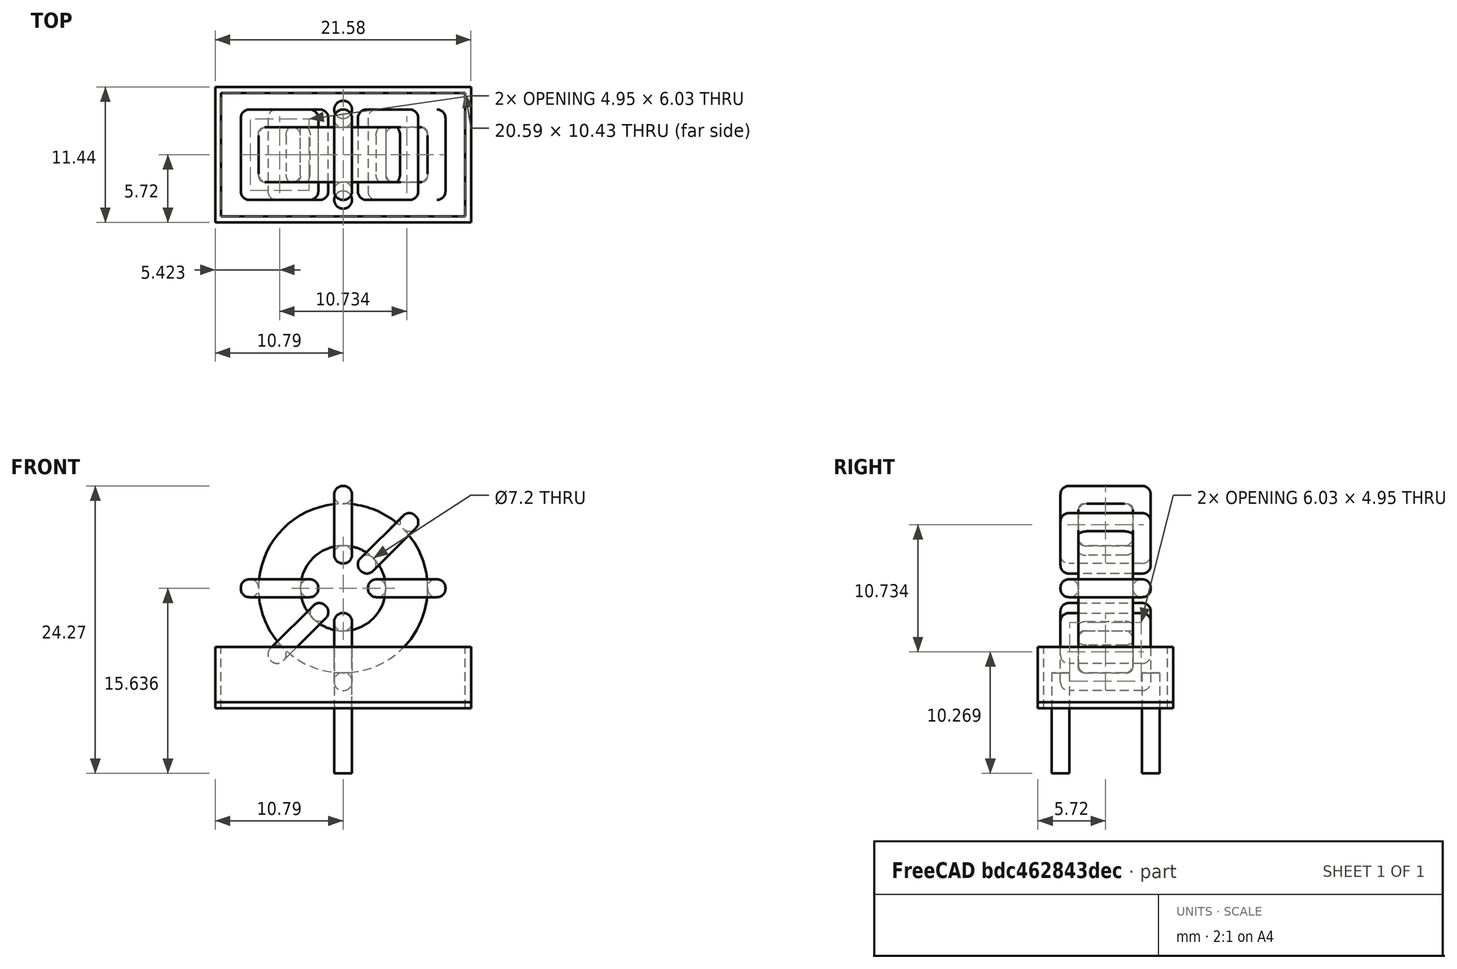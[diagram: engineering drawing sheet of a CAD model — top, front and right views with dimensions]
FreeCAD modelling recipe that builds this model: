
FCSTD DOCUMENT  (FreeCAD 0.16R6703 (Git))
Label: L_Toroid_Vertical_L21.6mm_W11.4mm_P7.62mm_Pulse_KM-3
License: All rights reserved
LicenseURL: http://en.wikipedia.org/wiki/All_rights_reserved
objects: Sketcher::SketchObject×8, PartDesign::Pad×8, PartDesign::Fillet×5, Spreadsheet::Sheet×1
note: 29 computed .brp shape members not serialized (recipe doc carries the construction recipe); baked Part::Feature solids carry a one-line shape summary decoded from their .brp

FEATURE [Spreadsheet::Sheet] Spreadsheet  label="dimensions"
  cells = A1=Wx; B1(Wx)=17.272; C1(WW)=7.196666666666666; D1(iWx)=21.59; A2=Wy; B2(Wy)=7.62; D2(iWy)=11.43; A3=RM; B3(RMx)=7.62; C3(RMy)=0; A4=d_wire; B4(d_wire)=1.5; A5=H; B5(H)=21.59; A6=offsetx; B6(offsetx)=10.795
FEATURE [Sketcher::SketchObject] Sketch
  Placement = pos=(0,-3.81,0) rot=(1,0,0;1.5708rad)
  expr: Placement.Base.y = -Spreadsheet.RMx / 2
  expr: Constraints[0] = Spreadsheet.Wx / 2 - Spreadsheet.d_wire
  expr: Constraints[4] = Spreadsheet.WW / 2
  expr: Constraints[2] = Spreadsheet.Wx / 2 + Spreadsheet.d_wire + 0.5
  sketch-geometry (2):
    g0: Circle CenterX=0 CenterY=10.636 CenterZ=0 NormalX=0 NormalY=0 NormalZ=1 Radius=7.136
    g1: Circle CenterX=0 CenterY=10.636 CenterZ=0 NormalX=0 NormalY=0 NormalZ=1 Radius=3.59833
  constraints (5):
    c: Radius(g0) = 7.136
    c: DistanceX(g-1,g0) = 0
    c: DistanceY(g-1,g0) = 10.636
    c: Coincident(g1,g0)
    c: Radius(g1) = 3.59833
FEATURE [PartDesign::Pad] Pad
  Length = 4.62
  Length2 = 100
  Midplane = true
  Placement = pos=(0,-3.81,0) rot=(1,0,0;1.5708rad)
  Sketch = -> Sketch
  Type = 0
  expr: Length = Spreadsheet.Wy - 2 * Spreadsheet.d_wire
FEATURE [Sketcher::SketchObject] Sketch001
  Placement = pos=(0,0,2) rot=(0,0,1;0rad)
  expr: Placement.Base.z = 0.5 + Spreadsheet.d_wire
  expr: Constraints[4] = Spreadsheet.RMy
  expr: Constraints[2] = -Spreadsheet.RMx
  expr: Constraints[1] = Spreadsheet.d_wire / 2
  sketch-geometry (2):
    g0: Circle CenterX=0 CenterY=0 CenterZ=0 NormalX=0 NormalY=0 NormalZ=1 Radius=0.75
    g1: Circle CenterX=0 CenterY=-7.62 CenterZ=0 NormalX=0 NormalY=0 NormalZ=1 Radius=0.75
  constraints (5):
    c: Equal(g0,g1)
    c: Radius(g0) = 0.75
    c: DistanceY(g-1,g1) = -7.62
    c: Coincident(g0,g-1)
    c: DistanceX(g-1,g1) = 0
FEATURE [PartDesign::Pad] Pad001
  Length = 1.5
  Length2 = 7
  Placement = pos=(0,0,2) rot=(0,0,1;0rad)
  Reversed = true
  Sketch = -> Sketch001
  Type = 4
  expr: Length2 = 5.5 + Spreadsheet.d_wire
  expr: Length = Spreadsheet.d_wire
FEATURE [PartDesign::Fillet] Fillet
  Base = -> Pad [Edge6,Edge3,Edge2]
  Placement = pos=(0,-3.81,0) rot=(1,0,0;1.5708rad)
  Radius = 0.5
FEATURE [Sketcher::SketchObject] Sketch003
  Placement = pos=(0,0,10.636) rot=(1,0,0;3.14159rad)
  expr: Constraints[18] = Spreadsheet.d_wire
  expr: Constraints[16] = Spreadsheet.d_wire
  expr: Constraints[19] = Spreadsheet.d_wire
  expr: Constraints[17] = Spreadsheet.d_wire
  expr: Placement.Base.y = -1 * (Spreadsheet.RMx - Spreadsheet.Wy) / 2
  expr: Constraints[21] = (Spreadsheet.Wx - Spreadsheet.WW) / 2 - Spreadsheet.d_wire
  expr: Constraints[22] = Spreadsheet.Wx / 2 - Spreadsheet.d_wire
  expr: Constraints[43] = Spreadsheet.d_wire
  expr: Constraints[48] = Spreadsheet.Wx - Spreadsheet.d_wire * 2
  expr: Constraints[49] = Spreadsheet.Wy
  expr: Placement.Base.z = Spreadsheet.Wx / 2 + Spreadsheet.d_wire + 0.5
  sketch-geometry (16):
    g0: LineSegment StartX=-2.09833 StartY=0 StartZ=0 EndX=-8.636 EndY=0 EndZ=0
    g1: LineSegment StartX=-8.636 StartY=0 StartZ=0 EndX=-8.636 EndY=7.62 EndZ=0
    g2: LineSegment StartX=-8.636 StartY=7.62 StartZ=0 EndX=-2.09833 EndY=7.62 EndZ=0
    g3: LineSegment StartX=-2.09833 StartY=7.62 StartZ=0 EndX=-2.09833 EndY=0 EndZ=0
    g4: LineSegment StartX=-7.136 StartY=6.12 StartZ=0 EndX=-3.59833 EndY=6.12 EndZ=0
    g5: LineSegment StartX=-3.59833 StartY=6.12 StartZ=0 EndX=-3.59833 EndY=1.5 EndZ=0
    g6: LineSegment StartX=-3.59833 StartY=1.5 StartZ=0 EndX=-7.136 EndY=1.5 EndZ=0
    g7: LineSegment StartX=-7.136 StartY=1.5 StartZ=0 EndX=-7.136 EndY=6.12 EndZ=0
    g8: LineSegment StartX=2.09833 StartY=7.62 StartZ=0 EndX=8.636 EndY=7.62 EndZ=0
    g9: LineSegment StartX=8.636 StartY=7.62 StartZ=0 EndX=8.636 EndY=0 EndZ=0
    g10: LineSegment StartX=8.636 StartY=0 StartZ=0 EndX=2.09833 EndY=0 EndZ=0
    g11: LineSegment StartX=2.09833 StartY=0 StartZ=0 EndX=2.09833 EndY=7.62 EndZ=0
    g12: LineSegment StartX=3.59833 StartY=6.12 StartZ=0 EndX=7.136 EndY=6.12 EndZ=0
    g13: LineSegment StartX=7.136 StartY=6.12 StartZ=0 EndX=7.136 EndY=1.5 EndZ=0
    g14: LineSegment StartX=7.136 StartY=1.5 StartZ=0 EndX=3.59833 EndY=1.5 EndZ=0
    g15: LineSegment StartX=3.59833 StartY=1.5 StartZ=0 EndX=3.59833 EndY=6.12 EndZ=0
  constraints (50):
    c: Horizontal(g0)
    c: Coincident(g1,g0)
    c: Vertical(g1)
    c: Coincident(g2,g1)
    c: Horizontal(g2)
    c: Coincident(g3,g2)
    c: Coincident(g3,g0)
    c: Vertical(g3)
    c: Coincident(g4,g5)
    c: Coincident(g5,g6)
    c: Coincident(g6,g7)
    c: Coincident(g7,g4)
    c: Horizontal(g4)
    c: Horizontal(g6)
    c: Vertical(g5)
    c: Vertical(g7)
    c: DistanceX(g1,g4) = 1.5
    c: DistanceY(g4,g1) = 1.5
    c: DistanceX(g5,g0) = 1.5
    c: DistanceY(g0,g5) = 1.5
    c: DistanceY(g-1,g0) = 0
    c: DistanceX(g6,g6) = 3.53767
    c: DistanceX(g6,g-1) = 7.136
    c: Coincident(g8,g9)
    c: Coincident(g9,g10)
    c: Coincident(g10,g11)
    c: Coincident(g11,g8)
    c: Horizontal(g8)
    c: Horizontal(g10)
    c: Vertical(g9)
    c: Vertical(g11)
    c: Coincident(g12,g13)
    c: Coincident(g13,g14)
    c: Coincident(g14,g15)
    c: Coincident(g15,g12)
    c: Horizontal(g12)
    c: Horizontal(g14)
    c: Vertical(g13)
    c: Vertical(g15)
    c: DistanceY(g8,g2) = 0
    c: DistanceY(g10,g0) = 0
    c: DistanceY(g14,g5) = 0
    c: DistanceY(g12,g4) = 0
    c: DistanceX(g8,g12) = 1.5
    c: Equal(g8,g2)
    c: Equal(g12,g4)
    c: Equal(g9,g1)
    c: Equal(g13,g7)
    c: DistanceX(g4,g12) = 14.272
    c: DistanceY(g0,g1) = 7.62
FEATURE [PartDesign::Pad] Pad002
  Length = 1.5
  Length2 = 100
  Midplane = true
  Placement = pos=(0,0,10.636) rot=(1,0,0;3.14159rad)
  Sketch = -> Sketch003
  Type = 0
  expr: Length = Spreadsheet.d_wire
FEATURE [PartDesign::Fillet] Fillet001
  Base = -> Pad002 [Edge38,Edge41,Edge42,Edge43,Edge29,Edge32,Edge33,Edge34,Edge25,Edge35,Edge36,Edge13,Edge14,Edge15,Edge16,Edge17,Edge18,Edge19,Edge1,Edge2,Edge3,Edge4,Edge5,Edge6,Edge7,Edge37,Edge39,Edge40,Edge20,Edge23,Edge24,Edge21,Edge22,Edge8,Edge9,Edge10,Edge11,Edge12,Edge26,Edge27,+8 more]
  Placement = pos=(0,0,10.636) rot=(1,0,0;3.14159rad)
  Radius = 0.705
  expr: Radius = Spreadsheet.d_wire * 0.47
FEATURE [Sketcher::SketchObject] Sketch004
  Placement = pos=(0,0,10.636) rot=(0.92388,0,0.382683;3.14159rad)
  expr: Constraints[18] = Spreadsheet.d_wire
  expr: Constraints[16] = Spreadsheet.d_wire
  expr: Constraints[19] = Spreadsheet.d_wire
  expr: Constraints[17] = Spreadsheet.d_wire
  expr: Placement.Base.y = -1 * (Spreadsheet.RMx - Spreadsheet.Wy) / 2
  expr: Constraints[21] = (Spreadsheet.Wx - Spreadsheet.WW) / 2 - Spreadsheet.d_wire
  expr: Constraints[22] = Spreadsheet.Wx / 2 - Spreadsheet.d_wire
  expr: Constraints[43] = Spreadsheet.d_wire
  expr: Constraints[48] = Spreadsheet.Wx - 2 * Spreadsheet.d_wire
  expr: Constraints[49] = Spreadsheet.Wy
  expr: Placement.Base.z = Spreadsheet.Wx / 2 + Spreadsheet.d_wire + 0.5
  sketch-geometry (16):
    g0: LineSegment StartX=-2.09833 StartY=0 StartZ=0 EndX=-8.636 EndY=0 EndZ=0
    g1: LineSegment StartX=-8.636 StartY=0 StartZ=0 EndX=-8.636 EndY=7.62 EndZ=0
    g2: LineSegment StartX=-8.636 StartY=7.62 StartZ=0 EndX=-2.09833 EndY=7.62 EndZ=0
    g3: LineSegment StartX=-2.09833 StartY=7.62 StartZ=0 EndX=-2.09833 EndY=0 EndZ=0
    g4: LineSegment StartX=-7.136 StartY=6.12 StartZ=0 EndX=-3.59833 EndY=6.12 EndZ=0
    g5: LineSegment StartX=-3.59833 StartY=6.12 StartZ=0 EndX=-3.59833 EndY=1.5 EndZ=0
    g6: LineSegment StartX=-3.59833 StartY=1.5 StartZ=0 EndX=-7.136 EndY=1.5 EndZ=0
    g7: LineSegment StartX=-7.136 StartY=1.5 StartZ=0 EndX=-7.136 EndY=6.12 EndZ=0
    g8: LineSegment StartX=2.09833 StartY=7.62 StartZ=0 EndX=8.636 EndY=7.62 EndZ=0
    g9: LineSegment StartX=8.636 StartY=7.62 StartZ=0 EndX=8.636 EndY=0 EndZ=0
    g10: LineSegment StartX=8.636 StartY=0 StartZ=0 EndX=2.09833 EndY=0 EndZ=0
    g11: LineSegment StartX=2.09833 StartY=0 StartZ=0 EndX=2.09833 EndY=7.62 EndZ=0
    g12: LineSegment StartX=3.59833 StartY=6.12 StartZ=0 EndX=7.136 EndY=6.12 EndZ=0
    g13: LineSegment StartX=7.136 StartY=6.12 StartZ=0 EndX=7.136 EndY=1.5 EndZ=0
    g14: LineSegment StartX=7.136 StartY=1.5 StartZ=0 EndX=3.59833 EndY=1.5 EndZ=0
    g15: LineSegment StartX=3.59833 StartY=1.5 StartZ=0 EndX=3.59833 EndY=6.12 EndZ=0
  constraints (50):
    c: Horizontal(g0)
    c: Coincident(g1,g0)
    c: Vertical(g1)
    c: Coincident(g2,g1)
    c: Horizontal(g2)
    c: Coincident(g3,g2)
    c: Coincident(g3,g0)
    c: Vertical(g3)
    c: Coincident(g4,g5)
    c: Coincident(g5,g6)
    c: Coincident(g6,g7)
    c: Coincident(g7,g4)
    c: Horizontal(g4)
    c: Horizontal(g6)
    c: Vertical(g5)
    c: Vertical(g7)
    c: DistanceX(g1,g4) = 1.5
    c: DistanceY(g4,g1) = 1.5
    c: DistanceX(g5,g0) = 1.5
    c: DistanceY(g0,g5) = 1.5
    c: DistanceY(g-1,g0) = 0
    c: DistanceX(g6,g6) = 3.53767
    c: DistanceX(g6,g-1) = 7.136
    c: Coincident(g8,g9)
    c: Coincident(g9,g10)
    c: Coincident(g10,g11)
    c: Coincident(g11,g8)
    c: Horizontal(g8)
    c: Horizontal(g10)
    c: Vertical(g9)
    c: Vertical(g11)
    c: Coincident(g12,g13)
    c: Coincident(g13,g14)
    c: Coincident(g14,g15)
    c: Coincident(g15,g12)
    c: Horizontal(g12)
    c: Horizontal(g14)
    c: Vertical(g13)
    c: Vertical(g15)
    c: DistanceY(g8,g2) = 0
    c: DistanceY(g10,g0) = 0
    c: DistanceY(g14,g5) = 0
    c: DistanceY(g12,g4) = 0
    c: DistanceX(g8,g12) = 1.5
    c: Equal(g8,g2)
    c: Equal(g12,g4)
    c: Equal(g9,g1)
    c: Equal(g13,g7)
    c: DistanceX(g4,g12) = 14.272
    c: DistanceY(g0,g1) = 7.62
FEATURE [PartDesign::Pad] Pad003
  Length = 1.5
  Length2 = 100
  Midplane = true
  Placement = pos=(0,0,10.636) rot=(0.92388,0,0.382683;3.14159rad)
  Sketch = -> Sketch004
  Type = 0
  expr: Length = Spreadsheet.d_wire
FEATURE [PartDesign::Fillet] Fillet002
  Base = -> Pad003 [Edge38,Edge41,Edge42,Edge43,Edge29,Edge32,Edge33,Edge34,Edge25,Edge35,Edge36,Edge13,Edge14,Edge15,Edge16,Edge17,Edge18,Edge19,Edge1,Edge2,Edge3,Edge4,Edge5,Edge6,Edge7,Edge37,Edge39,Edge40,Edge20,Edge23,Edge24,Edge21,Edge22,Edge8,Edge9,Edge10,Edge11,Edge12,Edge26,Edge27,+8 more]
  Placement = pos=(0,0,10.636) rot=(0.92388,0,0.382683;3.14159rad)
  Radius = 0.705
  expr: Radius = Spreadsheet.d_wire * 0.47
FEATURE [Sketcher::SketchObject] Sketch005
  Placement = pos=(0,0,10.636) rot=(0.92388,0,-0.382683;3.14159rad)
  expr: Constraints[18] = Spreadsheet.d_wire
  expr: Constraints[16] = Spreadsheet.d_wire
  expr: Constraints[19] = Spreadsheet.d_wire
  expr: Constraints[17] = Spreadsheet.d_wire
  expr: Placement.Base.y = -1 * (Spreadsheet.RMx - Spreadsheet.Wy) / 2
  expr: Constraints[21] = (Spreadsheet.Wx - Spreadsheet.WW) / 2 - Spreadsheet.d_wire
  expr: Constraints[22] = Spreadsheet.Wx / 2 - Spreadsheet.d_wire
  expr: Constraints[43] = Spreadsheet.d_wire
  expr: Constraints[48] = Spreadsheet.Wx - 2 * Spreadsheet.d_wire
  expr: Constraints[49] = Spreadsheet.Wy
  expr: Placement.Base.z = Spreadsheet.Wx / 2 + Spreadsheet.d_wire + 0.5
  sketch-geometry (16):
    g0: LineSegment StartX=-2.09833 StartY=0 StartZ=0 EndX=-8.636 EndY=0 EndZ=0
    g1: LineSegment StartX=-8.636 StartY=0 StartZ=0 EndX=-8.636 EndY=7.62 EndZ=0
    g2: LineSegment StartX=-8.636 StartY=7.62 StartZ=0 EndX=-2.09833 EndY=7.62 EndZ=0
    g3: LineSegment StartX=-2.09833 StartY=7.62 StartZ=0 EndX=-2.09833 EndY=0 EndZ=0
    g4: LineSegment StartX=-7.136 StartY=6.12 StartZ=0 EndX=-3.59833 EndY=6.12 EndZ=0
    g5: LineSegment StartX=-3.59833 StartY=6.12 StartZ=0 EndX=-3.59833 EndY=1.5 EndZ=0
    g6: LineSegment StartX=-3.59833 StartY=1.5 StartZ=0 EndX=-7.136 EndY=1.5 EndZ=0
    g7: LineSegment StartX=-7.136 StartY=1.5 StartZ=0 EndX=-7.136 EndY=6.12 EndZ=0
    g8: LineSegment StartX=2.09833 StartY=7.62 StartZ=0 EndX=8.636 EndY=7.62 EndZ=0
    g9: LineSegment StartX=8.636 StartY=7.62 StartZ=0 EndX=8.636 EndY=0 EndZ=0
    g10: LineSegment StartX=8.636 StartY=0 StartZ=0 EndX=2.09833 EndY=0 EndZ=0
    g11: LineSegment StartX=2.09833 StartY=0 StartZ=0 EndX=2.09833 EndY=7.62 EndZ=0
    g12: LineSegment StartX=3.59833 StartY=6.12 StartZ=0 EndX=7.136 EndY=6.12 EndZ=0
    g13: LineSegment StartX=7.136 StartY=6.12 StartZ=0 EndX=7.136 EndY=1.5 EndZ=0
    g14: LineSegment StartX=7.136 StartY=1.5 StartZ=0 EndX=3.59833 EndY=1.5 EndZ=0
    g15: LineSegment StartX=3.59833 StartY=1.5 StartZ=0 EndX=3.59833 EndY=6.12 EndZ=0
  constraints (50):
    c: Horizontal(g0)
    c: Coincident(g1,g0)
    c: Vertical(g1)
    c: Coincident(g2,g1)
    c: Horizontal(g2)
    c: Coincident(g3,g2)
    c: Coincident(g3,g0)
    c: Vertical(g3)
    c: Coincident(g4,g5)
    c: Coincident(g5,g6)
    c: Coincident(g6,g7)
    c: Coincident(g7,g4)
    c: Horizontal(g4)
    c: Horizontal(g6)
    c: Vertical(g5)
    c: Vertical(g7)
    c: DistanceX(g1,g4) = 1.5
    c: DistanceY(g4,g1) = 1.5
    c: DistanceX(g5,g0) = 1.5
    c: DistanceY(g0,g5) = 1.5
    c: DistanceY(g-1,g0) = 0
    c: DistanceX(g6,g6) = 3.53767
    c: DistanceX(g6,g-1) = 7.136
    c: Coincident(g8,g9)
    c: Coincident(g9,g10)
    c: Coincident(g10,g11)
    c: Coincident(g11,g8)
    c: Horizontal(g8)
    c: Horizontal(g10)
    c: Vertical(g9)
    c: Vertical(g11)
    c: Coincident(g12,g13)
    c: Coincident(g13,g14)
    c: Coincident(g14,g15)
    c: Coincident(g15,g12)
    c: Horizontal(g12)
    c: Horizontal(g14)
    c: Vertical(g13)
    c: Vertical(g15)
    c: DistanceY(g8,g2) = 0
    c: DistanceY(g10,g0) = 0
    c: DistanceY(g14,g5) = 0
    c: DistanceY(g12,g4) = 0
    c: DistanceX(g8,g12) = 1.5
    c: Equal(g8,g2)
    c: Equal(g12,g4)
    c: Equal(g9,g1)
    c: Equal(g13,g7)
    c: DistanceX(g4,g12) = 14.272
    c: DistanceY(g0,g1) = 7.62
FEATURE [PartDesign::Pad] Pad004
  Length = 1.5
  Length2 = 100
  Midplane = true
  Placement = pos=(0,0,10.636) rot=(0.92388,0,-0.382683;3.14159rad)
  Sketch = -> Sketch005
  Type = 0
  expr: Length = Spreadsheet.d_wire
FEATURE [PartDesign::Fillet] Fillet003
  Base = -> Pad004 [Edge38,Edge41,Edge42,Edge43,Edge29,Edge32,Edge33,Edge34,Edge25,Edge35,Edge36,Edge13,Edge14,Edge15,Edge16,Edge17,Edge18,Edge19,Edge1,Edge2,Edge3,Edge4,Edge5,Edge6,Edge7,Edge37,Edge39,Edge40,Edge20,Edge23,Edge24,Edge21,Edge22,Edge8,Edge9,Edge10,Edge11,Edge12,Edge26,Edge27,+8 more]
  Placement = pos=(0,0,10.636) rot=(0.92388,0,-0.382683;3.14159rad)
  Radius = 0.705
  expr: Radius = Spreadsheet.d_wire * 0.47
FEATURE [Sketcher::SketchObject] Sketch006
  Placement = pos=(0,0,10.636) rot=(0.707107,0,0.707107;3.14159rad)
  expr: Constraints[18] = Spreadsheet.d_wire
  expr: Constraints[16] = Spreadsheet.d_wire
  expr: Constraints[19] = Spreadsheet.d_wire
  expr: Constraints[17] = Spreadsheet.d_wire
  expr: Placement.Base.y = -1 * (Spreadsheet.RMx - Spreadsheet.Wy) / 2
  expr: Constraints[21] = (Spreadsheet.Wx - Spreadsheet.WW) / 2 - Spreadsheet.d_wire
  expr: Constraints[22] = Spreadsheet.Wx / 2 - Spreadsheet.d_wire
  expr: Constraints[43] = Spreadsheet.d_wire
  expr: Constraints[48] = Spreadsheet.Wx - Spreadsheet.d_wire * 2
  expr: Constraints[49] = Spreadsheet.Wy
  expr: Placement.Base.z = Spreadsheet.Wx / 2 + Spreadsheet.d_wire + 0.5
  sketch-geometry (16):
    g0: LineSegment StartX=-2.09833 StartY=0 StartZ=0 EndX=-8.636 EndY=0 EndZ=0
    g1: LineSegment StartX=-8.636 StartY=0 StartZ=0 EndX=-8.636 EndY=7.62 EndZ=0
    g2: LineSegment StartX=-8.636 StartY=7.62 StartZ=0 EndX=-2.09833 EndY=7.62 EndZ=0
    g3: LineSegment StartX=-2.09833 StartY=7.62 StartZ=0 EndX=-2.09833 EndY=0 EndZ=0
    g4: LineSegment StartX=-7.136 StartY=6.12 StartZ=0 EndX=-3.59833 EndY=6.12 EndZ=0
    g5: LineSegment StartX=-3.59833 StartY=6.12 StartZ=0 EndX=-3.59833 EndY=1.5 EndZ=0
    g6: LineSegment StartX=-3.59833 StartY=1.5 StartZ=0 EndX=-7.136 EndY=1.5 EndZ=0
    g7: LineSegment StartX=-7.136 StartY=1.5 StartZ=0 EndX=-7.136 EndY=6.12 EndZ=0
    g8: LineSegment StartX=2.09833 StartY=7.62 StartZ=0 EndX=8.636 EndY=7.62 EndZ=0
    g9: LineSegment StartX=8.636 StartY=7.62 StartZ=0 EndX=8.636 EndY=0 EndZ=0
    g10: LineSegment StartX=8.636 StartY=0 StartZ=0 EndX=2.09833 EndY=0 EndZ=0
    g11: LineSegment StartX=2.09833 StartY=0 StartZ=0 EndX=2.09833 EndY=7.62 EndZ=0
    g12: LineSegment StartX=3.59833 StartY=6.12 StartZ=0 EndX=7.136 EndY=6.12 EndZ=0
    g13: LineSegment StartX=7.136 StartY=6.12 StartZ=0 EndX=7.136 EndY=1.5 EndZ=0
    g14: LineSegment StartX=7.136 StartY=1.5 StartZ=0 EndX=3.59833 EndY=1.5 EndZ=0
    g15: LineSegment StartX=3.59833 StartY=1.5 StartZ=0 EndX=3.59833 EndY=6.12 EndZ=0
  constraints (50):
    c: Horizontal(g0)
    c: Coincident(g1,g0)
    c: Vertical(g1)
    c: Coincident(g2,g1)
    c: Horizontal(g2)
    c: Coincident(g3,g2)
    c: Coincident(g3,g0)
    c: Vertical(g3)
    c: Coincident(g4,g5)
    c: Coincident(g5,g6)
    c: Coincident(g6,g7)
    c: Coincident(g7,g4)
    c: Horizontal(g4)
    c: Horizontal(g6)
    c: Vertical(g5)
    c: Vertical(g7)
    c: DistanceX(g1,g4) = 1.5
    c: DistanceY(g4,g1) = 1.5
    c: DistanceX(g5,g0) = 1.5
    c: DistanceY(g0,g5) = 1.5
    c: DistanceY(g-1,g0) = 0
    c: DistanceX(g6,g6) = 3.53767
    c: DistanceX(g6,g-1) = 7.136
    c: Coincident(g8,g9)
    c: Coincident(g9,g10)
    c: Coincident(g10,g11)
    c: Coincident(g11,g8)
    c: Horizontal(g8)
    c: Horizontal(g10)
    c: Vertical(g9)
    c: Vertical(g11)
    c: Coincident(g12,g13)
    c: Coincident(g13,g14)
    c: Coincident(g14,g15)
    c: Coincident(g15,g12)
    c: Horizontal(g12)
    c: Horizontal(g14)
    c: Vertical(g13)
    c: Vertical(g15)
    c: DistanceY(g8,g2) = 0
    c: DistanceY(g10,g0) = 0
    c: DistanceY(g14,g5) = 0
    c: DistanceY(g12,g4) = 0
    c: DistanceX(g8,g12) = 1.5
    c: Equal(g8,g2)
    c: Equal(g12,g4)
    c: Equal(g9,g1)
    c: Equal(g13,g7)
    c: DistanceX(g4,g12) = 14.272
    c: DistanceY(g0,g1) = 7.62
FEATURE [PartDesign::Pad] Pad005
  Length = 1.5
  Length2 = 100
  Midplane = true
  Placement = pos=(0,0,10.636) rot=(0.707107,0,0.707107;3.14159rad)
  Sketch = -> Sketch006
  Type = 0
  expr: Length = Spreadsheet.d_wire
FEATURE [PartDesign::Fillet] Fillet004
  Base = -> Pad005 [Edge38,Edge41,Edge42,Edge43,Edge29,Edge32,Edge33,Edge34,Edge25,Edge35,Edge36,Edge13,Edge14,Edge15,Edge16,Edge17,Edge18,Edge19,Edge1,Edge2,Edge3,Edge4,Edge5,Edge6,Edge7,Edge37,Edge39,Edge40,Edge20,Edge23,Edge24,Edge21,Edge22,Edge8,Edge9,Edge10,Edge11,Edge12,Edge26,Edge27,+8 more]
  Placement = pos=(0,0,10.636) rot=(0.707107,0,0.707107;3.14159rad)
  Radius = 0.705
  expr: Radius = Spreadsheet.d_wire * 0.47
FEATURE [Sketcher::SketchObject] Sketch007
  Placement = pos=(0,0,0.5) rot=(0,0,1;0rad)
  expr: Placement.Base.z = 0.5
  expr: Constraints[11] = Spreadsheet.iWx / 2
  expr: Constraints[10] = (Spreadsheet.iWy - Spreadsheet.RMx) / 2
  expr: Constraints[9] = Spreadsheet.iWy
  expr: Constraints[8] = Spreadsheet.iWx
  sketch-geometry (4):
    g0: LineSegment StartX=-10.795 StartY=1.905 StartZ=0 EndX=10.795 EndY=1.905 EndZ=0
    g1: LineSegment StartX=10.795 StartY=1.905 StartZ=0 EndX=10.795 EndY=-9.525 EndZ=0
    g2: LineSegment StartX=10.795 StartY=-9.525 StartZ=0 EndX=-10.795 EndY=-9.525 EndZ=0
    g3: LineSegment StartX=-10.795 StartY=-9.525 StartZ=0 EndX=-10.795 EndY=1.905 EndZ=0
  constraints (12):
    c: Coincident(g0,g1)
    c: Coincident(g1,g2)
    c: Coincident(g2,g3)
    c: Coincident(g3,g0)
    c: Horizontal(g0)
    c: Horizontal(g2)
    c: Vertical(g1)
    c: Vertical(g3)
    c: DistanceX(g0,g0) = 21.59
    c: DistanceY(g3,g3) = 11.43
    c: DistanceY(g-1,g0) = 1.905
    c: DistanceX(g0,g-1) = 10.795
FEATURE [PartDesign::Pad] Pad006
  Length = 0.5
  Length2 = 100
  Placement = pos=(0,0,0.5) rot=(0,0,1;0rad)
  Sketch = -> Sketch007
  Type = 0
FEATURE [Sketcher::SketchObject] Sketch008
  Placement = pos=(0,0,0.5) rot=(0,0,1;0rad)
  expr: Constraints[8] = Spreadsheet.iWx
  expr: Constraints[9] = Spreadsheet.iWy
  expr: Constraints[10] = (Spreadsheet.iWy - Spreadsheet.RMx) / 2
  expr: Placement.Base.z = 0.5
  expr: Constraints[21] = 0.5
  expr: Constraints[11] = Spreadsheet.iWx / 2
  sketch-geometry (8):
    g0: LineSegment StartX=-10.795 StartY=1.905 StartZ=0 EndX=10.795 EndY=1.905 EndZ=0
    g1: LineSegment StartX=10.795 StartY=1.905 StartZ=0 EndX=10.795 EndY=-9.525 EndZ=0
    g2: LineSegment StartX=10.795 StartY=-9.525 StartZ=0 EndX=-10.795 EndY=-9.525 EndZ=0
    g3: LineSegment StartX=-10.795 StartY=-9.525 StartZ=0 EndX=-10.795 EndY=1.905 EndZ=0
    g4: LineSegment StartX=-10.295 StartY=1.405 StartZ=0 EndX=10.295 EndY=1.405 EndZ=0
    g5: LineSegment StartX=10.295 StartY=1.405 StartZ=0 EndX=10.295 EndY=-9.025 EndZ=0
    g6: LineSegment StartX=10.295 StartY=-9.025 StartZ=0 EndX=-10.295 EndY=-9.025 EndZ=0
    g7: LineSegment StartX=-10.295 StartY=-9.025 StartZ=0 EndX=-10.295 EndY=1.405 EndZ=0
  constraints (24):
    c: Coincident(g0,g1)
    c: Coincident(g1,g2)
    c: Coincident(g2,g3)
    c: Coincident(g3,g0)
    c: Horizontal(g0)
    c: Horizontal(g2)
    c: Vertical(g1)
    c: Vertical(g3)
    c: DistanceX(g0,g0) = 21.59
    c: DistanceY(g3,g3) = 11.43
    c: DistanceY(g-1,g0) = 1.905
    c: DistanceX(g0,g-1) = 10.795
    c: Coincident(g4,g5)
    c: Coincident(g5,g6)
    c: Coincident(g6,g7)
    c: Coincident(g7,g4)
    c: Horizontal(g4)
    c: Horizontal(g6)
    c: Vertical(g5)
    c: Vertical(g7)
    c: DistanceX(g5,g1) = 0.5
    c: DistanceY(g1,g5) = 0.5
    c: DistanceX(g0,g4) = 0.5
    c: DistanceY(g4,g0) = 0.5
FEATURE [PartDesign::Pad] Pad007
  Length = 5.1816
  Length2 = 100
  Placement = pos=(0,0,0.5) rot=(0,0,1;0rad)
  Sketch = -> Sketch008
  Type = 0
  expr: Length = Spreadsheet.Wx * 0.3
